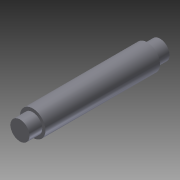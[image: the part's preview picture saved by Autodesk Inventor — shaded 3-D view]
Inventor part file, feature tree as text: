
AUTODESK INVENTOR PART (.ipt)
format: ipt  version: 2012 (Build 160160000, 160)  size: 89,600 bytes
history: native  units: in
note: dims shown in document units (in); Inventor stores cm internally (conversion verified against a paired STEP export)
features: extrude x5, sketch x3, plane x2
ambient origin geometry x8: Origin, YZ Plane, XZ Plane, XY Plane, X Axis, Y Axis, Z Axis, Center Point
bodies: Solid1 (feature_tree)
feature tree (10):
  extrude  "Extrusion1"  Depth=3.25in TaperAngle=0.0deg
  plane  "Work Plane4"
  sketch  "Sketch4"  dims[d14=-0.5in d17=-0.5in]
  plane  "Work Plane5"
  sketch  "Sketch5"  dims[d24=0.375in d25=1.0in d26=0.0in d27=0.375in d28=1.0in d29=0.0in d30=0.25in d31=0.0in d32=0.25in d33=0.0in]
  extrude  "Extrusion6"  [1 undecoded]
  extrude  "Extrusion7"  Depth=1.0in TaperAngle=0.0deg
  extrude  "Extrusion8"  Depth=0.375in
  extrude  "Extrusion9"  Depth=1.0in TaperAngle=0.0deg
  sketch  "Sketch1"  dims[d0=0.5in d1=3.25in d2=0.0in]
note: 1 required parameter value undecoded (feature->parameter linkage not recoverable at this tier; creation-order binding heuristic only, values carry confidence <= 0.55)
